# Revit family: LAMP_OCULT SYSTEM PENDULAR
name_source: partatom
category: Luminarias
revit_build: Autodesk Revit 2015 (Build: 20140606_1530(x64)
units: mm (PartAtom-declared; Revit-internal decimal feet)

## types (8) — shared parameters
CRI = 80
Comentarios de tipo = Availability of changing profile version and height when placed in project.
Diameter = 35 mm  [stored 0.114829 ft]
Elevación por defecto = 1219 mm
Fabricante = LAMP
Gear = Electronic
Height = 400 mm  [stored 1.31234 ft]
IEE = A+
Installation instructions = https://www.lamp.es
Insulation class = I
LED Lifetime = 50.000 L90
Lamp = HIGH POWER LED
Last update = 14/06/2019
Luminaire type = Pendular downlight
MacAdam = 3
Manufacturer URL = http://www.lamp.es
Manufacturer country = Spain
Manufacturer name = LAMP
Material suspension = Panel de metal
Model explanation = Availability of changing profile version and height when placed in project.
Plum = 6 W
Power = 4 W
Power Supply = 220-240V 50/60Hz
Product URL = https://www.lamp.es
Product datasheet = http://www.lamp.es
Protection rating = IP20
Type = HIGH POWER CREE
Weight = 0.83 kg

## per-type parameters (varying)
| type | Descripción | Efficacy | Finish | Initial color | Initial intensity | Material perfil | Modelo | Photometric web file | Product code |
| 331LM 3000 FLOOD BLACK | OCULT SYS. PEND.VERT. 500 WW FL BK/BK. | 55 lm/W | Texturised black RAL 9011 | 3000 K | 331 lm | LAMP_Aluminio Ocult Pendular NG | OS1PV05FL830NBB | Modelo pendular : 331LM 3000 FLOOD BLACK | OS1PV05FL830NBB |
| 331LM 3000 FLOOD WHITE | OCULT SYS. PEND.VERT. 500 WW FL BK/WH. | 55 lm/W | Texturised matt white | 3000 K | 331 lm | LAMP_Aluminio Ocult Pendular BL | OS1PV05FL830NBW | Modelo pendular : 331LM 3000 FLOOD WHITE | OS1PV05FL830NBW |
| 349LM 4000 FLOOD BLACK | OCULT SYS. PEND.VERT. 500 NW FL BK/BK. | 58 lm/W | Texturised black RAL 9011 | 4000 K | 349 lm | LAMP_Aluminio Ocult Pendular NG | OS1PV05FL840NBB | Modelo pendular : 349LM 4000 FLOOD BLACK | OS1PV05FL840NBB |
| 349LM 4000 FLOOD WHITE | OCULT SYS. PEND.VERT. 500 NW FL BK/WH. | 58 lm/W | Texturised matt white | 4000 K | 349 lm | LAMP_Aluminio Ocult Pendular BL | OS1PV05FL840NBW | Modelo pendular : 349LM 4000 FLOOD WHITE | OS1PV05FL840NBW |
| 414LM 3000 SPOT BLACK | OCULT SYS. PEND.VERT. 500 WW SP BK/BK. | 69 lm/W | Texturised black RAL 9011 | 3000 K | 414 lm | LAMP_Aluminio Ocult Pendular NG | OS1PV05SP830NBB | Modelo pendular : 414LM 3000 SPOT BLACK | OS1PV05SP830NBB |
| 414LM 3000 SPOT WHITE | OCULT SYS. PEND.VERT. 500 WW SP BK/WH. | 69 lm/W | Texturised matt white | 3000 K | 414 lm | LAMP_Aluminio Ocult Pendular BL | OS1PV05SP830NBW | Modelo pendular : 414LM 3000 SPOT WHITE | OS1PV05SP830NBW |
| 443LM 4000 SPOT BLACK | OCULT SYS. PEND.VERT. 500 NW SP BK/BK. | 74 lm/W | Texturised black RAL 9011 | 4000 K | 443 lm | LAMP_Aluminio Ocult Pendular NG | OS1PV05SP840NBB | Modelo pendular : 443LM 4000 SPOT BLACK | OS1PV05SP840NBB |
| 443LM 4000 SPOT WHITE | OCULT SYS. PEND.VERT. 500 NW SP BK/WH. | 74 lm/W | Texturised matt white | 4000 K | 443 lm | LAMP_Aluminio Ocult Pendular BL | OS1PV05SP840NBW | Modelo pendular : 443LM 4000 SPOT WHITE | OS1PV05SP840NBW |

note: [stored X ft] marks values corroborated as IEEE doubles in the binary element streams (Revit-internal decimal feet)
